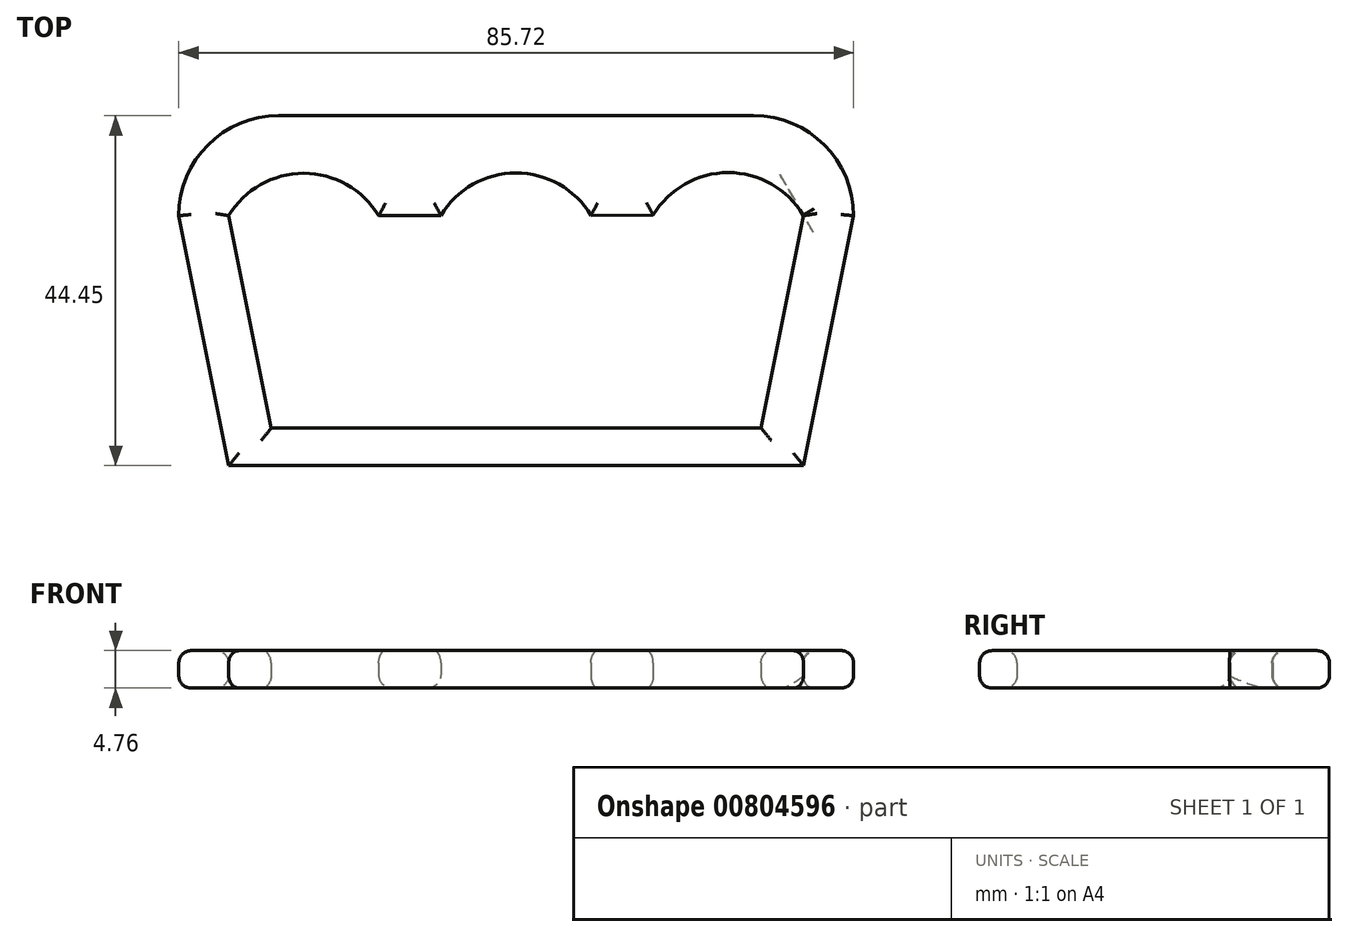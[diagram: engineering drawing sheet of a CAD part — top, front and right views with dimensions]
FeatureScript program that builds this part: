
annotation { "Feature Type Name" : "Feature", "Feature Type Description" : "" }
export const myFeature = defineFeature(function(context is Context, id is Id, definition is map)
    precondition{}
    {
        {
            var Q0;
            Q0=qCreatedBy(makeId("Top.planeOp"),FACE);
            var sketch = newSketch(context, id + "F0", { "sketchPlane" : qUnion([Q0])});
            skLineSegment(sketch, "E0.bottom", {"start": v(-36.51, -18.26) * mm, "end": v(36.51, -18.26) * mm});
            skLineSegment(sketch, "E0.top", {"start": v(-30.16, 26.2) * mm, "end": v(30.16, 26.2) * mm});
            skLineSegment(sketch, "E0.left", {"start": v(-42.86, 13.5) * mm, "end": v(-42.86, 13.5) * mm});
            skLineSegment(sketch, "E0.right", {"start": v(42.86, 13.5) * mm, "end": v(42.86, 13.5) * mm});
            skLineSegment(sketch, "E1.top", {"start": v(-31.11, -13.5) * mm, "end": v(31.11, -13.5) * mm});
            skPoint(sketch, "E1.middle", {"position": v(0, 0) * mm});
            skArc(sketch, "E2", {"start": v(-17.46, 13.5) * mm, "mid": v(-26.99, 18.88) * mm, "end": v(-36.51, 13.5) * mm});
            skLineSegment(sketch, "E3", {"start": v(-36.51, 13.5) * mm, "end": v(-31.11, -13.5) * mm});
            skLineSegment(sketch, "E4", {"start": v(-42.86, 13.5) * mm, "end": v(-36.51, -18.26) * mm});
            skLineSegment(sketch, "E5.MirrorCS", {"start": v(36.51, 13.5) * mm, "end": v(31.11, -13.5) * mm});
            skLineSegment(sketch, "E6.MirrorCS", {"start": v(42.86, 13.5) * mm, "end": v(36.51, -18.26) * mm});
            skArc(sketch, "E7.1.0.0", {"start": v(9.5, 13.54) * mm, "mid": v(-0.03, 18.93) * mm, "end": v(-9.55, 13.54) * mm});
            skArc(sketch, "E7.2.0.0", {"start": v(36.46, 13.58) * mm, "mid": v(26.94, 18.97) * mm, "end": v(17.41, 13.58) * mm});
            skLineSegment(sketch, "E7.direction1", {"start": v(-36.51, 13.5) * mm, "end": v(-9.55, 13.54) * mm, "construction": true});
            skLineSegment(sketch, "E8", {"start": v(36.46, 13.58) * mm, "end": v(36.51, 13.5) * mm});
            skLineSegment(sketch, "E9", {"start": v(-17.46, 13.5) * mm, "end": v(-9.55, 13.54) * mm});
            skLineSegment(sketch, "E10", {"start": v(9.5, 13.54) * mm, "end": v(17.41, 13.58) * mm});
            skPoint(sketch, "E11.visualSharp", {"position": v(-42.86, 26.2) * mm});
            skArc(sketch, "E11.filletArc", {"start": v(-30.16, 26.2) * mm, "mid": v(-39.14, 22.47) * mm, "end": v(-42.86, 13.5) * mm});
            skPoint(sketch, "E12.visualSharp", {"position": v(42.86, 26.2) * mm});
            skArc(sketch, "E12.filletArc", {"start": v(42.86, 13.5) * mm, "mid": v(39.14, 22.47) * mm, "end": v(30.16, 26.2) * mm});
            skSolve(sketch);
        }
        {
            var Q0;
            Q0=makeQuery(id+"F0.imprint","IMPRINT",FACE,{"disambiguationData":[TD([[makeQuery(id+"F0.imprint","IMPRINT",EDGE,{"derivedFrom":sQuery(id+"F0.wireOp",EDGE,"E0.bottom")}),1.0]])]});
            extrude(context, id + "F1", {"entities" : qUnion([Q0]), "depth" : 4.76 * mm, "offsetDistance" : 25.4 * mm});
        }
        {
            var Q0;
            Q0=makeQuery(id+"F1.opExtrude","CAP_EDGE",EDGE,{"disambiguationData":[OSD([sQuery(id+"F0.wireOp",EDGE,"E4")])],"isStart":false});
            var Q1;
            Q1=makeQuery(id+"F1.opExtrude","CAP_EDGE",EDGE,{"disambiguationData":[OSD([sQuery(id+"F0.wireOp",EDGE,"E11.filletArc")])],"isStart":false});
            var Q2;
            Q2=makeQuery(id+"F1.opExtrude","CAP_EDGE",EDGE,{"disambiguationData":[OSD([sQuery(id+"F0.wireOp",EDGE,"E0.top")])],"isStart":false});
            var Q3;
            Q3=makeQuery(id+"F1.opExtrude","CAP_EDGE",EDGE,{"disambiguationData":[OSD([sQuery(id+"F0.wireOp",EDGE,"E12.filletArc")])],"isStart":false});
            var Q4;
            Q4=makeQuery(id+"F1.opExtrude","CAP_EDGE",EDGE,{"disambiguationData":[OSD([sQuery(id+"F0.wireOp",EDGE,"E6.MirrorCS")])],"isStart":false});
            var Q5;
            Q5=makeQuery(id+"F1.opExtrude","CAP_EDGE",EDGE,{"disambiguationData":[OSD([sQuery(id+"F0.wireOp",EDGE,"E0.bottom")])],"isStart":false});
            var Q6;
            Q6=makeQuery(id+"F1.opExtrude","CAP_EDGE",EDGE,{"disambiguationData":[OSD([sQuery(id+"F0.wireOp",EDGE,"E0.bottom")])],"isStart":true});
            var Q7;
            Q7=makeQuery(id+"F1.opExtrude","CAP_EDGE",EDGE,{"disambiguationData":[OSD([sQuery(id+"F0.wireOp",EDGE,"E3")])],"isStart":false});
            var Q8;
            Q8=makeQuery(id+"F1.opExtrude","CAP_EDGE",EDGE,{"disambiguationData":[OSD([sQuery(id+"F0.wireOp",EDGE,"E1.top")])],"isStart":false});
            var Q9;
            Q9=makeQuery(id+"F1.opExtrude","CAP_EDGE",EDGE,{"disambiguationData":[OSD([sQuery(id+"F0.wireOp",EDGE,"E2")])],"isStart":false});
            var Q10;
            Q10=makeQuery(id+"F1.opExtrude","CAP_EDGE",EDGE,{"disambiguationData":[OSD([sQuery(id+"F0.wireOp",EDGE,"E9")])],"isStart":false});
            var Q11;
            Q11=makeQuery(id+"F1.opExtrude","CAP_EDGE",EDGE,{"disambiguationData":[OSD([sQuery(id+"F0.wireOp",EDGE,"E7.1.0.0")])],"isStart":false});
            var Q12;
            Q12=makeQuery(id+"F1.opExtrude","CAP_EDGE",EDGE,{"disambiguationData":[OSD([sQuery(id+"F0.wireOp",EDGE,"E10")])],"isStart":false});
            var Q13;
            Q13=makeQuery(id+"F1.opExtrude","CAP_EDGE",EDGE,{"disambiguationData":[OSD([sQuery(id+"F0.wireOp",EDGE,"E7.2.0.0")])],"isStart":false});
            var Q14;
            Q14=makeQuery(id+"F1.opExtrude","CAP_EDGE",EDGE,{"disambiguationData":[OSD([sQuery(id+"F0.wireOp",EDGE,"E5.MirrorCS")])],"isStart":false});
            var Q15;
            Q15=makeQuery(id+"F1.opExtrude","CAP_FACE",FACE,{"disambiguationData":[OSD([sQuery(id+"F0.wireOp",EDGE,"E0.bottom"),sQuery(id+"F0.wireOp",EDGE,"E0.top"),sQuery(id+"F0.wireOp",EDGE,"E1.top"),sQuery(id+"F0.wireOp",EDGE,"E2"),sQuery(id+"F0.wireOp",EDGE,"E3"),sQuery(id+"F0.wireOp",EDGE,"E4"),sQuery(id+"F0.wireOp",EDGE,"E5.MirrorCS"),sQuery(id+"F0.wireOp",EDGE,"E6.MirrorCS"),sQuery(id+"F0.wireOp",EDGE,"E7.1.0.0"),sQuery(id+"F0.wireOp",EDGE,"E7.2.0.0"),sQuery(id+"F0.wireOp",EDGE,"E8"),sQuery(id+"F0.wireOp",EDGE,"E9"),sQuery(id+"F0.wireOp",EDGE,"E10"),sQuery(id+"F0.wireOp",EDGE,"E11.filletArc"),sQuery(id+"F0.wireOp",EDGE,"E12.filletArc")])],"isStart":false});
            var Q16;
            Q16=makeQuery(id+"F1.opExtrude","CAP_EDGE",EDGE,{"disambiguationData":[OSD([sQuery(id+"F0.wireOp",EDGE,"E12.filletArc")])],"isStart":true});
            var Q17;
            Q17=makeQuery(id+"F1.opExtrude","CAP_EDGE",EDGE,{"disambiguationData":[OSD([sQuery(id+"F0.wireOp",EDGE,"E0.top")])],"isStart":true});
            var Q18;
            Q18=makeQuery(id+"F1.opExtrude","CAP_EDGE",EDGE,{"disambiguationData":[OSD([sQuery(id+"F0.wireOp",EDGE,"E6.MirrorCS")])],"isStart":true});
            var Q19;
            Q19=makeQuery(id+"F1.opExtrude","CAP_EDGE",EDGE,{"disambiguationData":[OSD([sQuery(id+"F0.wireOp",EDGE,"E5.MirrorCS")])],"isStart":true});
            var Q20;
            Q20=makeQuery(id+"F1.opExtrude","CAP_EDGE",EDGE,{"disambiguationData":[OSD([sQuery(id+"F0.wireOp",EDGE,"E1.top")])],"isStart":true});
            var Q21;
            Q21=makeQuery(id+"F1.opExtrude","CAP_EDGE",EDGE,{"disambiguationData":[OSD([sQuery(id+"F0.wireOp",EDGE,"E3")])],"isStart":true});
            var Q22;
            Q22=makeQuery(id+"F1.opExtrude","CAP_EDGE",EDGE,{"disambiguationData":[OSD([sQuery(id+"F0.wireOp",EDGE,"E4")])],"isStart":true});
            var Q23;
            Q23=makeQuery(id+"F1.opExtrude","CAP_EDGE",EDGE,{"disambiguationData":[OSD([sQuery(id+"F0.wireOp",EDGE,"E11.filletArc")])],"isStart":true});
            var Q24;
            Q24=makeQuery(id+"F1.opExtrude","CAP_EDGE",EDGE,{"disambiguationData":[OSD([sQuery(id+"F0.wireOp",EDGE,"E7.1.0.0")])],"isStart":true});
            var Q25;
            Q25=makeQuery(id+"F1.opExtrude","CAP_EDGE",EDGE,{"disambiguationData":[OSD([sQuery(id+"F0.wireOp",EDGE,"E10")])],"isStart":true});
            var Q26;
            Q26=makeQuery(id+"F1.opExtrude","CAP_EDGE",EDGE,{"disambiguationData":[OSD([sQuery(id+"F0.wireOp",EDGE,"E7.2.0.0")])],"isStart":true});
            var Q27;
            Q27=makeQuery(id+"F1.opExtrude","CAP_EDGE",EDGE,{"disambiguationData":[OSD([sQuery(id+"F0.wireOp",EDGE,"E2")])],"isStart":true});
            fillet(context, id + "F2", {"entities" : qUnion([Q0, Q1, Q2, Q3, Q4, Q5, Q6, Q7, Q8, Q9, Q10, Q11, Q12, Q13, Q14, Q15, Q16, Q17, Q18, Q19, Q20, Q21, Q22, Q23, Q24, Q25, Q26, Q27]), "radius" : 1.59 * mm, "tangentPropagation" : true, "allowEdgeOverflow" : false});
        }
    });
